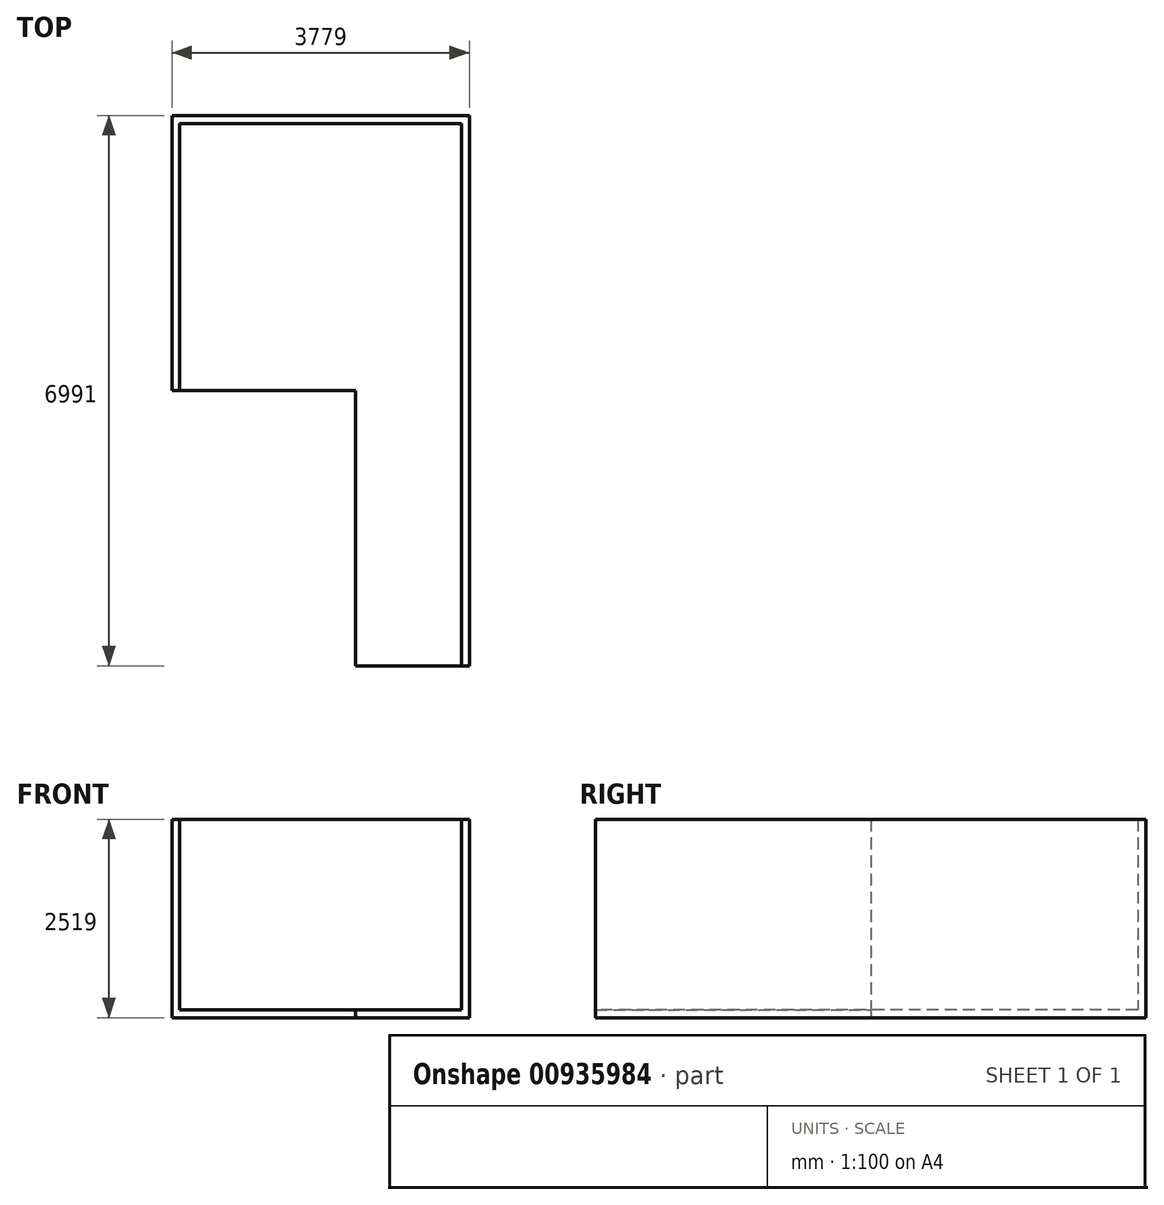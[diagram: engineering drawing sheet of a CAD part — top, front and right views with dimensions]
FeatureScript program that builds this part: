
annotation { "Feature Type Name" : "Feature", "Feature Type Description" : "" }
export const myFeature = defineFeature(function(context is Context, id is Id, definition is map)
    precondition{}
    {
        {
            var Q0;
            Q0=qCreatedBy(makeId("Top.planeOp"),FACE);
            var sketch = newSketch(context, id + "F0", { "sketchPlane" : qUnion([Q0])});
            skLineSegment(sketch, "E0.bottom", {"start": v(1889.5, -1745.5) * mm, "end": v(-1889.5, -1745.5) * mm});
            skLineSegment(sketch, "E0.top", {"start": v(1889.5, 1745.5) * mm, "end": v(-1889.5, 1745.5) * mm});
            skLineSegment(sketch, "E0.left", {"start": v(1889.5, -1745.5) * mm, "end": v(1889.5, 1745.5) * mm});
            skLineSegment(sketch, "E0.right", {"start": v(-1889.5, -1745.5) * mm, "end": v(-1889.5, 1745.5) * mm});
            skPoint(sketch, "E0.middle", {"position": v(0, 0) * mm});
            skSolve(sketch);
        }
        {
            var Q0;
            Q0=makeQuery(id+"F0.imprint","IMPRINT",FACE,{"disambiguationData":[TD([[makeQuery(id+"F0.imprint","IMPRINT",EDGE,{"derivedFrom":sQuery(id+"F0.wireOp",EDGE,"E0.bottom")}),-1.0]])]});
            extrude(context, id + "F1", {"entities" : qUnion([Q0]), "depth" : 100 * mm, "offsetDistance" : 25 * mm});
        }
        {
            var Q0;
            Q0=makeQuery(id+"F1.opExtrude","CAP_FACE",FACE,{"disambiguationData":[OSD([sQuery(id+"F0.wireOp",EDGE,"E0.bottom"),sQuery(id+"F0.wireOp",EDGE,"E0.top"),sQuery(id+"F0.wireOp",EDGE,"E0.left"),sQuery(id+"F0.wireOp",EDGE,"E0.right")])],"isStart":false});
            var sketch = newSketch(context, id + "F2", { "sketchPlane" : qUnion([Q0])});
            skLineSegment(sketch, "E1.bottom", {"start": v(-1889.5, 1745.5) * mm, "end": v(-1789.5, 1745.5) * mm});
            skLineSegment(sketch, "E1.top", {"start": v(-1889.5, -1745.5) * mm, "end": v(-1789.5, -1745.5) * mm});
            skLineSegment(sketch, "E1.left", {"start": v(-1889.5, 1745.5) * mm, "end": v(-1889.5, -1745.5) * mm});
            skLineSegment(sketch, "E1.right", {"start": v(-1789.5, 1645.5) * mm, "end": v(-1789.5, -1745.5) * mm});
            skLineSegment(sketch, "E2.bottom", {"start": v(1889.5, 1745.5) * mm, "end": v(1789.5, 1745.5) * mm});
            skLineSegment(sketch, "E2.top", {"start": v(1889.5, -1745.5) * mm, "end": v(1789.5, -1745.5) * mm});
            skLineSegment(sketch, "E2.left", {"start": v(1889.5, 1745.5) * mm, "end": v(1889.5, -1745.5) * mm});
            skLineSegment(sketch, "E2.right", {"start": v(1789.5, 1645.5) * mm, "end": v(1789.5, -1645.5) * mm});
            skLineSegment(sketch, "E3.bottom", {"start": v(-1789.5, 1745.5) * mm, "end": v(1789.5, 1745.5) * mm});
            skLineSegment(sketch, "E3.top", {"start": v(-1789.5, 1645.5) * mm, "end": v(1789.5, 1645.5) * mm});
            skLineSegment(sketch, "E4.right", {"start": v(1789.5, -1745.5) * mm, "end": v(1789.5, -1645.5) * mm});
            skSolve(sketch);
        }
        {
            var Q0;
            Q0=makeQuery(id+"F2.imprint","IMPRINT",FACE,{"disambiguationData":[TD([[makeQuery(id+"F2.imprint","IMPRINT",EDGE,{"derivedFrom":sQuery(id+"F2.wireOp",EDGE,"E1.bottom")}),1.0]])]});
            extrude(context, id + "F3", {"entities" : qUnion([Q0]), "operationType" : NewBodyOperationType.ADD, "depth" : 2419 * mm, "offsetDistance" : 25 * mm});
        }
        {
            var Q0;
            Q0=makeQuery(id+"F3.boolean.opBoolean","MERGE",FACE,{"derivedFrom":[makeQuery(id+"F1.opExtrude","SWEPT_FACE",FACE,{"disambiguationData":[OSD([sQuery(id+"F0.wireOp",EDGE,"E0.bottom")])]}),makeQuery(id+"F3.opExtrude","SWEPT_FACE",FACE,{"disambiguationData":[OSD([sQuery(id+"F2.wireOp",EDGE,"E1.top")])]}),makeQuery(id+"F3.opExtrude","SWEPT_FACE",FACE,{"disambiguationData":[OSD([sQuery(id+"F2.wireOp",EDGE,"E2.top")])]})]});
            var sketch = newSketch(context, id + "F4", { "sketchPlane" : qUnion([Q0])});
            skLineSegment(sketch, "E5.bottom", {"start": v(1789.5, 2519) * mm, "end": v(1889.5, 2519) * mm});
            skLineSegment(sketch, "E5.right", {"start": v(1889.5, 2519) * mm, "end": v(1889.5, 0) * mm});
            skLineSegment(sketch, "E6", {"start": v(443.5, 100) * mm, "end": v(443.5, 0) * mm});
            skLineSegment(sketch, "E7", {"start": v(1789.5, 2519) * mm, "end": v(1789.5, 100) * mm});
            skLineSegment(sketch, "E8", {"start": v(1789.5, 100) * mm, "end": v(443.5, 100) * mm});
            skLineSegment(sketch, "E9", {"start": v(1889.5, 0) * mm, "end": v(443.5, 0) * mm});
            skSolve(sketch);
        }
        {
            var Q0;
            Q0=makeQuery(id+"F4.imprint","IMPRINT",FACE,{"disambiguationData":[TD([[makeQuery(id+"F4.imprint","IMPRINT",EDGE,{"derivedFrom":sQuery(id+"F4.wireOp",EDGE,"E5.bottom")}),1.0]])]});
            extrude(context, id + "F5", {"entities" : qUnion([Q0]), "operationType" : NewBodyOperationType.ADD, "depth" : 3500 * mm, "offsetDistance" : 25 * mm});
        }
    });
